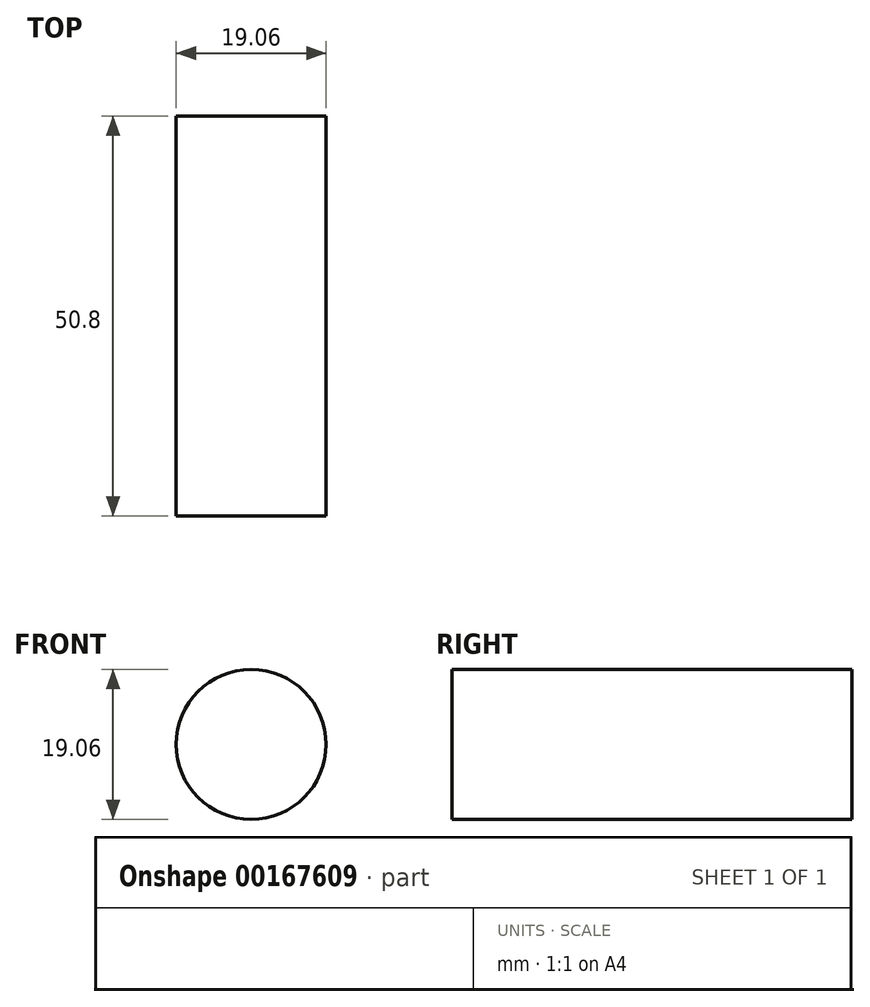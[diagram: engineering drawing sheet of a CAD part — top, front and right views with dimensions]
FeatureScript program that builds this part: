
annotation { "Feature Type Name" : "Feature", "Feature Type Description" : "" }
export const myFeature = defineFeature(function(context is Context, id is Id, definition is map)
    precondition{}
    {
        {
            var Q0;
            Q0=qCreatedBy(makeId("Front.planeOp"),FACE);
            var sketch = newSketch(context, id + "F0", { "sketchPlane" : qUnion([Q0])});
            skCircle(sketch, "E0", {"center": v(0, 0) * mm, "radius": 9.53 * mm});
            skSolve(sketch);
        }
        {
            var Q0;
            Q0=makeQuery(id+"F0.imprint","IMPRINT",FACE,{"disambiguationData":[TD([[makeQuery(id+"F0.imprint","IMPRINT",EDGE,{"derivedFrom":sQuery(id+"F0.wireOp",EDGE,"E0")}),1.0]])]});
            extrude(context, id + "F1", {"entities" : qUnion([Q0]), "depth" : 25.4 * mm});
        }
        {
            var Q0;
            Q0=makeQuery(id+"F1.opExtrude","CAP_FACE",FACE,{"disambiguationData":[OSD([sQuery(id+"F0.wireOp",EDGE,"E0")])],"isStart":false});
            extrude(context, id + "F2", {"entities" : qUnion([Q0]), "operationType" : NewBodyOperationType.ADD, "depth" : 25.4 * mm});
        }
    });
